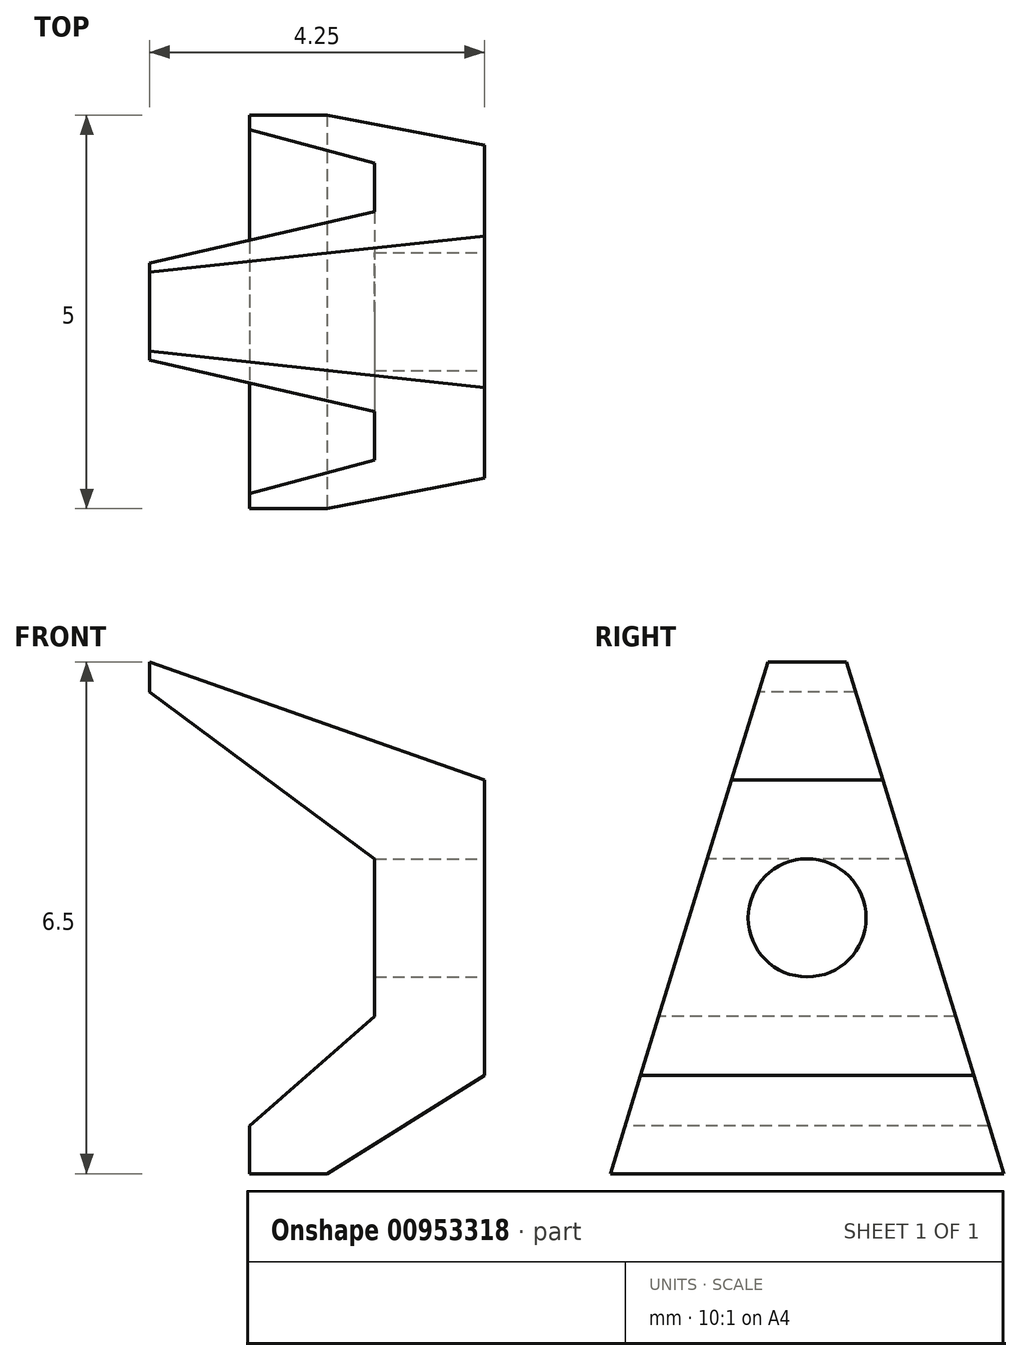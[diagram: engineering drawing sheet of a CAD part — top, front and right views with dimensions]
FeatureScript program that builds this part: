
annotation { "Feature Type Name" : "Feature", "Feature Type Description" : "" }
export const myFeature = defineFeature(function(context is Context, id is Id, definition is map)
    precondition{}
    {
        {
            var Q0;
            Q0=qCreatedBy(makeId("Right.planeOp"),FACE);
            var sketch = newSketch(context, id + "F0", { "sketchPlane" : qUnion([Q0])});
            skLineSegment(sketch, "E0", {"start": v(-0.5, 4) * mm, "end": v(-2.5, -2.5) * mm});
            skLineSegment(sketch, "E1", {"start": v(-2.5, -2.5) * mm, "end": v(2.5, -2.5) * mm});
            skLineSegment(sketch, "E2", {"start": v(2.5, -2.5) * mm, "end": v(0.5, 4) * mm});
            skLineSegment(sketch, "E3", {"start": v(0.5, 4) * mm, "end": v(-0.5, 4) * mm});
            skLineSegment(sketch, "E4", {"start": v(0, 4) * mm, "end": v(0, 0) * mm, "construction": true});
            skCircle(sketch, "E5", {"center": v(0, 0) * mm, "radius": 1 * mm, "construction": true});
            skSolve(sketch);
        }
        {
            var Q0;
            Q0 = qSketchRegion(id + "F0", true);
            extrude(context, id + "F1", {"entities" : qUnion([Q0]), "depth" : 4.25 * mm, "offsetDistance" : 25.4 * mm});
        }
        {
            var Q0;
            Q0=makeQuery(id+"F1.opExtrude","CAP_FACE",FACE,{"disambiguationData":[OSD([sQuery(id+"F0.wireOp",EDGE,"E0"),sQuery(id+"F0.wireOp",EDGE,"E1"),sQuery(id+"F0.wireOp",EDGE,"E2"),sQuery(id+"F0.wireOp",EDGE,"E3")])],"isStart":false});
            var sketch = newSketch(context, id + "F2", { "sketchPlane" : qUnion([Q0])});
            skCircle(sketch, "E6", {"center": v(0, 0.75) * mm, "radius": 0.75 * mm});
            skPoint(sketch, "E6.centerSnap0", {"position": v(-1.5, 0.75) * mm});
            skSolve(sketch);
        }
        {
            var Q0;
            Q0 = qSketchRegion(id + "F2", true);
            extrude(context, id + "F3", {"entities" : qUnion([Q0]), "operationType" : NewBodyOperationType.REMOVE, "endBound" : BoundingType.THROUGH_ALL, "oppositeDirection" : true, "depth" : 25.4 * mm, "offsetDistance" : 25.4 * mm});
        }
        {
            var Q0;
            Q0=qCreatedBy(makeId("Front.planeOp"),FACE);
            var sketch = newSketch(context, id + "F4", { "sketchPlane" : qUnion([Q0])});
            skLineSegment(sketch, "E7", {"start": v(0, 3.62) * mm, "end": v(2.86, 1.5) * mm});
            skLineSegment(sketch, "E8", {"start": v(2.86, 1.5) * mm, "end": v(2.86, -0.5) * mm});
            skLineSegment(sketch, "E9", {"start": v(2.86, -0.5) * mm, "end": v(1.27, -1.9) * mm});
            skLineSegment(sketch, "E10", {"start": v(1.27, -1.9) * mm, "end": v(1.27, -2.5) * mm});
            skLineSegment(sketch, "E11", {"start": v(1.27, -2.5) * mm, "end": v(0, -2.5) * mm});
            skLineSegment(sketch, "E12", {"start": v(0, -2.5) * mm, "end": v(0, 3.62) * mm});
            skLineSegment(sketch, "E13", {"start": v(4.25, 4) * mm, "end": v(0, 4) * mm});
            skLineSegment(sketch, "E14", {"start": v(0, 4) * mm, "end": v(4.25, 2.5) * mm});
            skLineSegment(sketch, "E15", {"start": v(4.25, 2.5) * mm, "end": v(4.25, 4) * mm});
            skLineSegment(sketch, "E16", {"start": v(4.25, -2.5) * mm, "end": v(2.25, -2.5) * mm});
            skLineSegment(sketch, "E17", {"start": v(2.25, -2.5) * mm, "end": v(4.25, -1.25) * mm});
            skLineSegment(sketch, "E18", {"start": v(4.25, -1.25) * mm, "end": v(4.25, -2.5) * mm});
            skSolve(sketch);
        }
        {
            var Q0;
            Q0 = qSketchRegion(id + "F4", true);
            extrude(context, id + "F5", {"entities" : qUnion([Q0]), "operationType" : NewBodyOperationType.REMOVE, "endBound" : BoundingType.SYMMETRIC, "oppositeDirection" : true, "depth" : 25.4 * mm, "offsetDistance" : 25.4 * mm});
        }
    });
